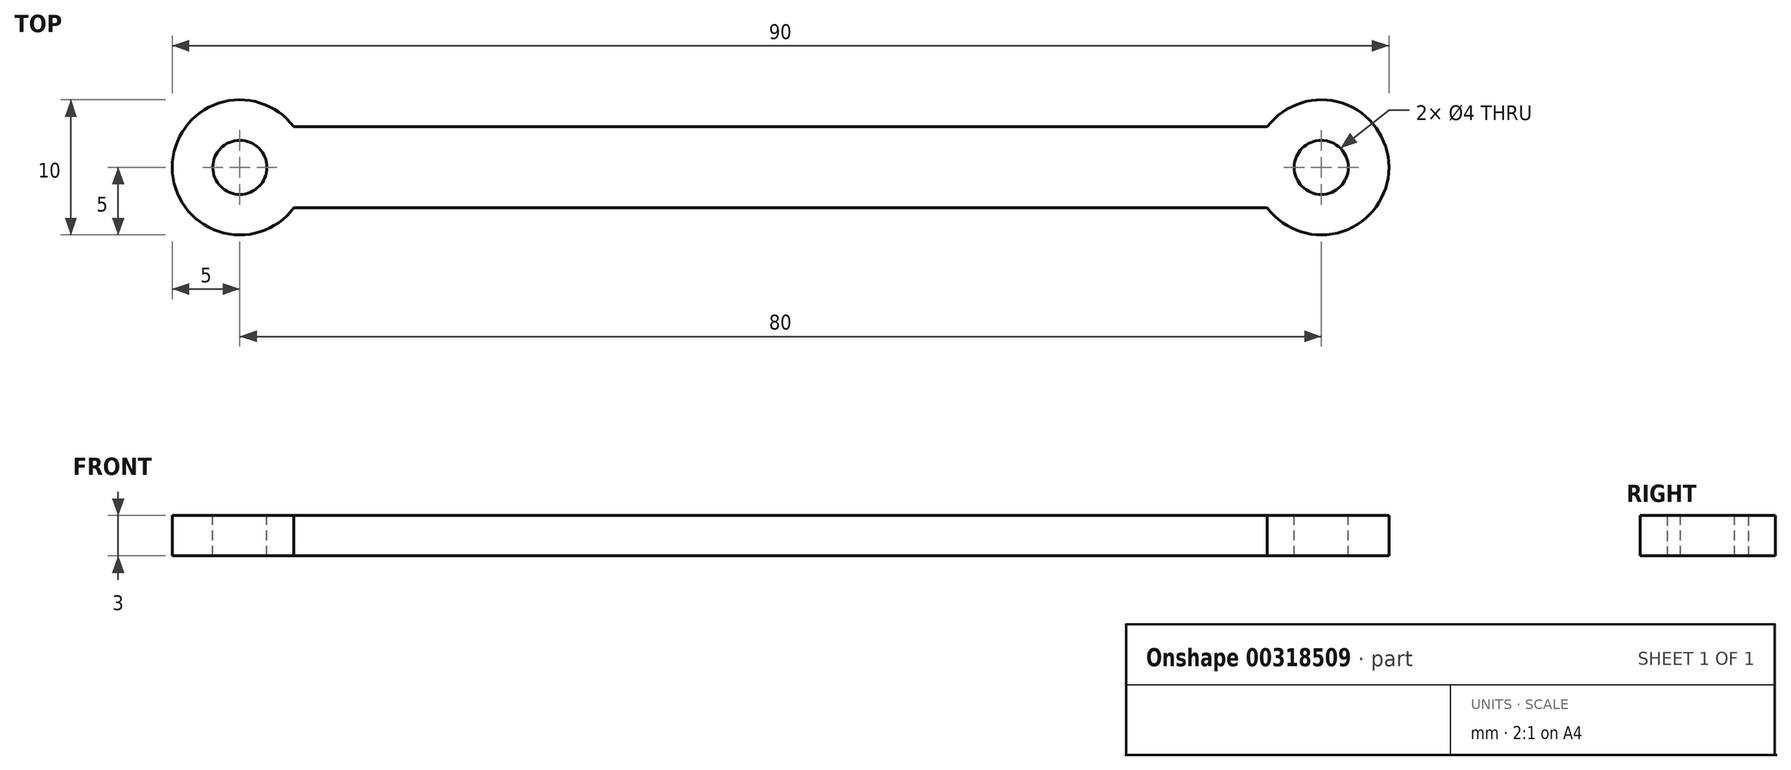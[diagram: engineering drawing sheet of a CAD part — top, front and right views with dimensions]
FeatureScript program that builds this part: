
annotation { "Feature Type Name" : "Feature", "Feature Type Description" : "" }
export const myFeature = defineFeature(function(context is Context, id is Id, definition is map)
    precondition{}
    {
        {
            var Q0;
            Q0=qCreatedBy(makeId("Top.planeOp"),FACE);
            var sketch = newSketch(context, id + "F0", { "sketchPlane" : qUnion([Q0])});
            skArc(sketch, "E0", {"start": v(-36, 3) * mm, "mid": v(-45, 0) * mm, "end": v(-36, -3) * mm});
            skArc(sketch, "E1", {"start": v(36, -3) * mm, "mid": v(45, 0) * mm, "end": v(36, 3) * mm});
            skLineSegment(sketch, "E2", {"start": v(-36, 3) * mm, "end": v(36, 3) * mm});
            skLineSegment(sketch, "E3", {"start": v(-36, -3) * mm, "end": v(36, -3) * mm});
            skSolve(sketch);
        }
        {
            var Q0;
            Q0 = qSketchRegion(id + "F0", true);
            extrude(context, id + "F1", {"entities" : qUnion([Q0]), "depth" : 3 * mm});
        }
        {
            var Q0;
            Q0=makeQuery(id+"F1.opExtrude","CAP_FACE",FACE,{"disambiguationData":[OSD([sQuery(id+"F0.wireOp",EDGE,"E0"),sQuery(id+"F0.wireOp",EDGE,"E1"),sQuery(id+"F0.wireOp",EDGE,"E2"),sQuery(id+"F0.wireOp",EDGE,"E3")])],"isStart":false});
            var sketch = newSketch(context, id + "F2", { "sketchPlane" : qUnion([Q0])});
            skCircle(sketch, "E4", {"center": v(-40, 0) * mm, "radius": 2 * mm});
            skCircle(sketch, "E5", {"center": v(40, 0) * mm, "radius": 2 * mm});
            skSolve(sketch);
        }
        {
            var Q0;
            Q0 = qSketchRegion(id + "F2", true);
            extrude(context, id + "F3", {"entities" : qUnion([Q0]), "operationType" : NewBodyOperationType.REMOVE, "oppositeDirection" : true, "depth" : 25 * mm});
        }
    });
